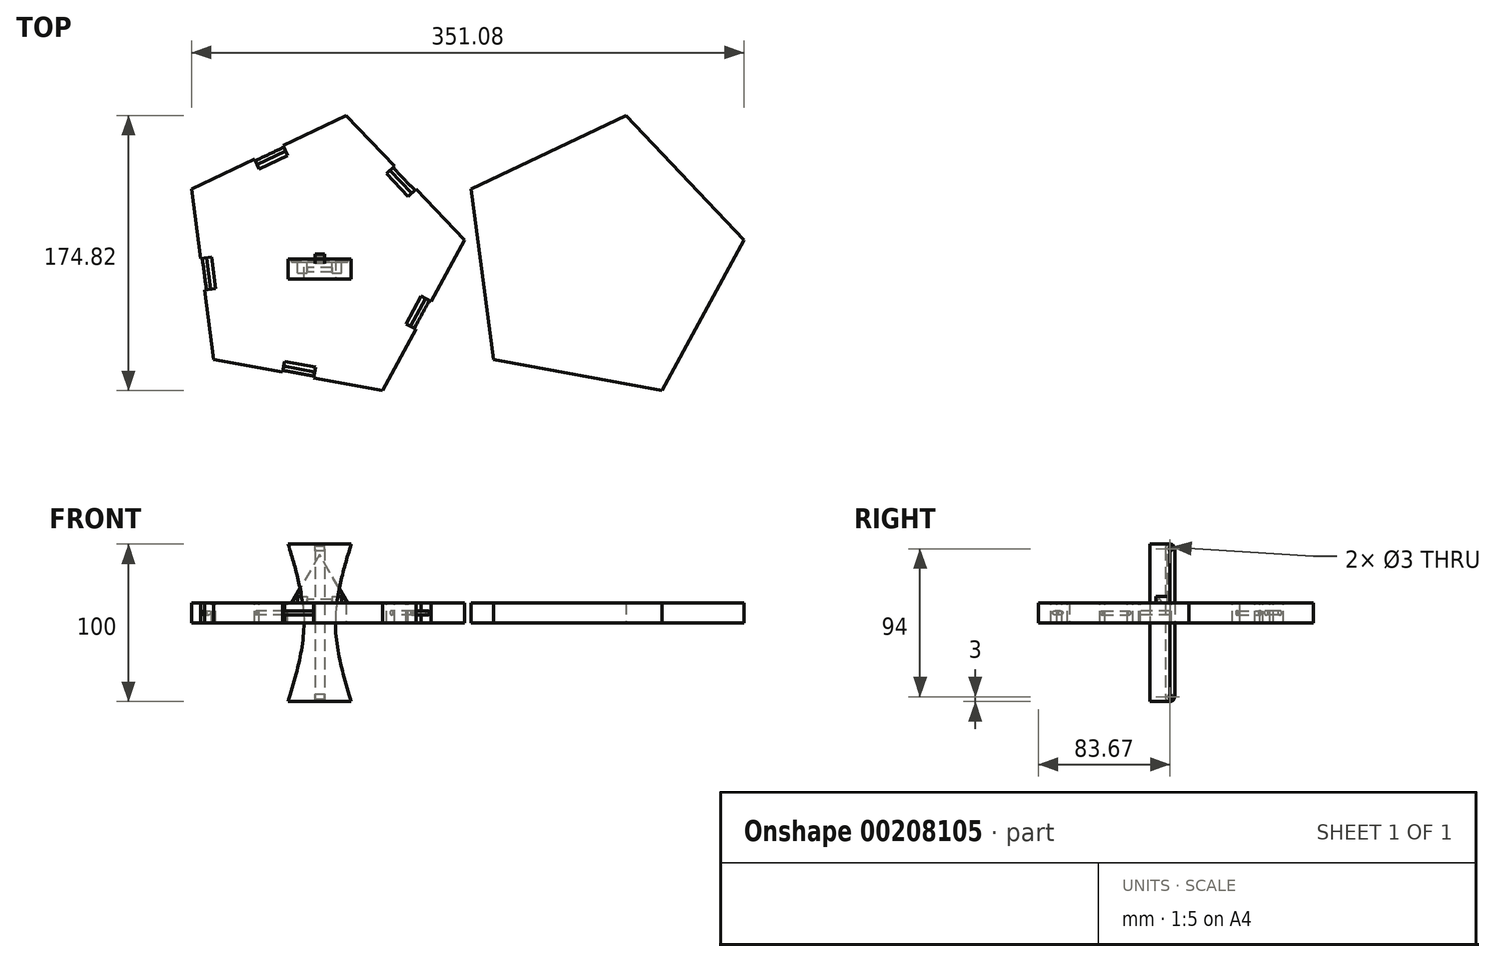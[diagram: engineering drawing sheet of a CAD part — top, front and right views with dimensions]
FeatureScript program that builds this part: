
annotation { "Feature Type Name" : "Feature", "Feature Type Description" : "" }
export const myFeature = defineFeature(function(context is Context, id is Id, definition is map)
    precondition{}
    {
        {
            var Q0;
            Q0=qCreatedBy(makeId("Top.planeOp"),FACE);
            var sketch = newSketch(context, id + "F0", { "sketchPlane" : qUnion([Q0])});
            skCircle(sketch, "E0.cCircle", {"center": v(0, 0) * mm, "radius": 75 * mm, "construction": true});
            skLineSegment(sketch, "E0.0", {"start": v(91.91, 12.1) * mm, "end": v(39.9, -83.67) * mm});
            skLineSegment(sketch, "E0.1", {"start": v(39.9, -83.67) * mm, "end": v(-67.25, -63.81) * mm});
            skLineSegment(sketch, "E0.2", {"start": v(-67.25, -63.81) * mm, "end": v(-81.47, 44.24) * mm});
            skLineSegment(sketch, "E0.3", {"start": v(-81.47, 44.24) * mm, "end": v(16.9, 91.15) * mm});
            skLineSegment(sketch, "E0.4", {"start": v(16.9, 91.15) * mm, "end": v(91.91, 12.1) * mm});
            skPoint(sketch, "E0.0.midPoint", {"position": v(65.91, -35.79) * mm});
            skSolve(sketch);
        }
        {
            var Q0;
            Q0=makeQuery(id+"F0.imprint","IMPRINT",FACE,{"disambiguationData":[TD([[makeQuery(id+"F0.imprint","IMPRINT",EDGE,{"derivedFrom":sQuery(id+"F0.wireOp",EDGE,"E0.0")}),-1.0]])]});
            extrude(context, id + "F1", {"entities" : qUnion([Q0]), "depth" : 12.7 * mm});
        }
        {
            var Q0;
            Q0=makeQuery(id+"F1.opExtrude","SWEPT_BODY",BODY,{"disambiguationData":[OSD([sQuery(id+"F0.wireOp",EDGE,"E0.0"),sQuery(id+"F0.wireOp",EDGE,"E0.1"),sQuery(id+"F0.wireOp",EDGE,"E0.2"),sQuery(id+"F0.wireOp",EDGE,"E0.3"),sQuery(id+"F0.wireOp",EDGE,"E0.4")])]});
            transform(context, id + "F2", {"entities" : qUnion([Q0]), "transformType" : TransformType.TRANSLATION_3D, "dx" : 177.7 * mm, "dy" : 0 * mm, "dz" : 0 * mm, "makeCopy" : true});
        }
        {
            var Q0;
            Q0=qCreatedBy(makeId("Front.planeOp"),FACE);
            var sketch = newSketch(context, id + "F3", { "sketchPlane" : qUnion([Q0])});
            skLineSegment(sketch, "E1", {"start": v(-25, 0) * mm, "end": v(25, 0) * mm});
            skLineSegment(sketch, "E2", {"start": v(25, 0) * mm, "end": v(0, 43.3) * mm});
            skLineSegment(sketch, "E3", {"start": v(0, 43.3) * mm, "end": v(-25, 0) * mm});
            skLineSegment(sketch, "E4", {"start": v(0, 43.3) * mm, "end": v(0, 0) * mm, "construction": true});
            skSolve(sketch);
        }
        {
            var Q0;
            Q0=makeQuery(id+"F3.imprint","IMPRINT",FACE,{"disambiguationData":[TD([[makeQuery(id+"F3.imprint","IMPRINT",EDGE,{"derivedFrom":sQuery(id+"F3.wireOp",EDGE,"E1")}),1.0]])]});
            extrude(context, id + "F4", {"entities" : qUnion([Q0]), "depth" : 2 * mm});
        }
        {
            var Q0;
            Q0=qCreatedBy(makeId("Right.planeOp"),FACE);
            var sketch = newSketch(context, id + "F5", { "sketchPlane" : qUnion([Q0])});
            skCircle(sketch, "E5", {"center": v(-7, 13.3) * mm, "radius": 1.5 * mm});
            skSolve(sketch);
        }
        {
            var Q0;
            Q0=makeQuery(id+"F4.opExtrude","CAP_FACE",FACE,{"disambiguationData":[OSD([sQuery(id+"F3.wireOp",EDGE,"E1"),sQuery(id+"F3.wireOp",EDGE,"E2"),sQuery(id+"F3.wireOp",EDGE,"E3")])],"isStart":false});
            var sketch = newSketch(context, id + "F6", { "sketchPlane" : qUnion([Q0])});
            skLineSegment(sketch, "E6.bottom", {"start": v(-14, 16.8) * mm, "end": v(-8, 16.8) * mm});
            skLineSegment(sketch, "E6.top", {"start": v(-14, 9.8) * mm, "end": v(-8, 9.8) * mm});
            skLineSegment(sketch, "E6.left", {"start": v(-14, 16.8) * mm, "end": v(-14, 9.8) * mm});
            skLineSegment(sketch, "E6.right", {"start": v(-8, 16.8) * mm, "end": v(-8, 9.8) * mm});
            skLineSegment(sketch, "E7.bottom", {"start": v(8, 16.8) * mm, "end": v(14, 16.8) * mm});
            skLineSegment(sketch, "E7.top", {"start": v(8, 9.8) * mm, "end": v(14, 9.8) * mm});
            skLineSegment(sketch, "E7.left", {"start": v(8, 16.8) * mm, "end": v(8, 9.8) * mm});
            skLineSegment(sketch, "E7.right", {"start": v(14, 16.8) * mm, "end": v(14, 9.8) * mm});
            skLineSegment(sketch, "E8", {"start": v(8, 13.3) * mm, "end": v(14, 13.3) * mm, "construction": true});
            skSolve(sketch);
        }
        {
            var Q0;
            Q0=makeQuery(id+"F6.imprint","IMPRINT",FACE,{"disambiguationData":[TD([[makeQuery(id+"F6.imprint","IMPRINT",EDGE,{"derivedFrom":sQuery(id+"F6.wireOp",EDGE,"E6.bottom")}),-1.0]])]});
            var Q1;
            Q1=makeQuery(id+"F6.imprint","IMPRINT",FACE,{"disambiguationData":[TD([[makeQuery(id+"F6.imprint","IMPRINT",EDGE,{"derivedFrom":sQuery(id+"F6.wireOp",EDGE,"E7.bottom")}),-1.0]])]});
            extrude(context, id + "F7", {"entities" : qUnion([Q0, Q1]), "operationType" : NewBodyOperationType.ADD, "depth" : 7 * mm});
        }
        {
            var Q0;
            Q0=makeQuery(id+"F5.imprint","IMPRINT",FACE,{"disambiguationData":[TD([[makeQuery(id+"F5.imprint","IMPRINT",EDGE,{"derivedFrom":sQuery(id+"F5.wireOp",EDGE,"E5")}),1.0]])]});
            extrude(context, id + "F8", {"entities" : qUnion([Q0]), "operationType" : NewBodyOperationType.ADD, "endBound" : BoundingType.SYMMETRIC, "depth" : 25 * mm});
        }
        {
            var Q0;
            Q0=makeQuery(id+"F1.opExtrude","CAP_FACE",FACE,{"disambiguationData":[OSD([sQuery(id+"F0.wireOp",EDGE,"E0.0"),sQuery(id+"F0.wireOp",EDGE,"E0.1"),sQuery(id+"F0.wireOp",EDGE,"E0.2"),sQuery(id+"F0.wireOp",EDGE,"E0.3"),sQuery(id+"F0.wireOp",EDGE,"E0.4")])],"isStart":false});
            var sketch = newSketch(context, id + "F9", { "sketchPlane" : qUnion([Q0])});
            skLineSegment(sketch, "E9", {"start": v(-75.66, 0.13) * mm, "end": v(-73.05, -19.7) * mm});
            skLineSegment(sketch, "E10", {"start": v(-73.05, -19.7) * mm, "end": v(-66.11, -18.79) * mm});
            skLineSegment(sketch, "E11", {"start": v(-66.11, -18.79) * mm, "end": v(-68.72, 1.04) * mm});
            skLineSegment(sketch, "E12", {"start": v(-75.66, 0.13) * mm, "end": v(-68.72, 1.04) * mm});
            skPoint(sketch, "E13.orphan", {"position": v(-73.05, 33.93) * mm});
            skLineSegment(sketch, "E14", {"start": v(-67.42, -8.87) * mm, "end": v(-74.36, -9.79) * mm, "construction": true});
            skLineSegment(sketch, "E15", {"start": v(-74.36, -9.79) * mm, "end": v(0, 0) * mm, "construction": true});
            skPoint(sketch, "E16.center", {"position": v(0, 0) * mm});
            skLineSegment(sketch, "E17.1.0", {"start": v(-23.5, -71.92) * mm, "end": v(-22.23, -65.04) * mm});
            skLineSegment(sketch, "E17.1.1", {"start": v(-2.56, -68.68) * mm, "end": v(-22.23, -65.04) * mm});
            skLineSegment(sketch, "E17.1.2", {"start": v(-3.84, -75.57) * mm, "end": v(-2.56, -68.68) * mm});
            skLineSegment(sketch, "E17.1.3", {"start": v(-23.5, -71.92) * mm, "end": v(-3.84, -75.57) * mm});
            skLineSegment(sketch, "E17.2.0", {"start": v(61.14, -44.58) * mm, "end": v(54.99, -41.24) * mm});
            skLineSegment(sketch, "E17.2.1", {"start": v(64.53, -23.66) * mm, "end": v(54.99, -41.24) * mm});
            skLineSegment(sketch, "E17.2.2", {"start": v(70.68, -27) * mm, "end": v(64.53, -23.66) * mm});
            skLineSegment(sketch, "E17.2.3", {"start": v(61.14, -44.58) * mm, "end": v(70.68, -27) * mm});
            skLineSegment(sketch, "E17.3.0", {"start": v(61.29, 44.37) * mm, "end": v(56.2, 39.55) * mm});
            skLineSegment(sketch, "E17.3.1", {"start": v(42.44, 54.06) * mm, "end": v(56.2, 39.55) * mm});
            skLineSegment(sketch, "E17.3.2", {"start": v(47.52, 58.88) * mm, "end": v(42.44, 54.06) * mm});
            skLineSegment(sketch, "E17.3.3", {"start": v(61.29, 44.37) * mm, "end": v(47.52, 58.88) * mm});
            skLineSegment(sketch, "E17.4.0", {"start": v(-23.26, 72) * mm, "end": v(-20.25, 65.68) * mm});
            skLineSegment(sketch, "E17.4.1", {"start": v(-38.3, 57.07) * mm, "end": v(-20.25, 65.68) * mm});
            skLineSegment(sketch, "E17.4.2", {"start": v(-41.31, 63.39) * mm, "end": v(-38.3, 57.07) * mm});
            skLineSegment(sketch, "E17.4.3", {"start": v(-23.26, 72) * mm, "end": v(-41.31, 63.39) * mm});
            skSolve(sketch);
        }
        {
            var Q0;
            Q0=makeQuery(id+"F9.imprint","IMPRINT",FACE,{"disambiguationData":[TD([[makeQuery(id+"F9.imprint","IMPRINT",EDGE,{"derivedFrom":sQuery(id+"F9.wireOp",EDGE,"E9")}),-1.0]])]});
            var Q1;
            Q1=makeQuery(id+"F9.imprint","IMPRINT",FACE,{"disambiguationData":[TD([[makeQuery(id+"F9.imprint","IMPRINT",EDGE,{"derivedFrom":sQuery(id+"F9.wireOp",EDGE,"E17.1.0")}),-1.0]])]});
            var Q2;
            Q2=makeQuery(id+"F9.imprint","IMPRINT",FACE,{"disambiguationData":[TD([[makeQuery(id+"F9.imprint","IMPRINT",EDGE,{"derivedFrom":sQuery(id+"F9.wireOp",EDGE,"E17.2.0")}),-1.0]])]});
            var Q3;
            Q3=makeQuery(id+"F9.imprint","IMPRINT",FACE,{"disambiguationData":[TD([[makeQuery(id+"F9.imprint","IMPRINT",EDGE,{"derivedFrom":sQuery(id+"F9.wireOp",EDGE,"E17.4.0")}),-1.0]])]});
            var Q4;
            Q4=makeQuery(id+"F9.imprint","IMPRINT",FACE,{"disambiguationData":[TD([[makeQuery(id+"F9.imprint","IMPRINT",EDGE,{"derivedFrom":sQuery(id+"F9.wireOp",EDGE,"E17.3.0")}),-1.0]])]});
            var Q5;
            Q5=makeQuery(id+"F1.opExtrude","CAP_FACE",FACE,{"disambiguationData":[OSD([sQuery(id+"F0.wireOp",EDGE,"E0.0"),sQuery(id+"F0.wireOp",EDGE,"E0.1"),sQuery(id+"F0.wireOp",EDGE,"E0.2"),sQuery(id+"F0.wireOp",EDGE,"E0.3"),sQuery(id+"F0.wireOp",EDGE,"E0.4")])],"isStart":true});
            extrude(context, id + "F10", {"entities" : qUnion([Q0, Q1, Q2, Q3, Q4]), "operationType" : NewBodyOperationType.REMOVE, "endBound" : BoundingType.UP_TO_SURFACE, "oppositeDirection" : true, "endBoundEntityFace" : qUnion([Q5]), "depth" : 25 * mm});
        }
        {
            var Q0;
            Q0=qCreatedBy(makeId("Right.planeOp"),FACE);
            var sketch = newSketch(context, id + "F11", { "sketchPlane" : qUnion([Q0])});
            skLineSegment(sketch, "E18", {"start": v(0, 0) * mm, "end": v(0, 99.53) * mm, "construction": true});
            skSolve(sketch);
        }
        {
            var Q0;
            Q0=makeQuery(id+"F10.boolean.opBoolean","COPY",FACE,{"derivedFrom":makeQuery(id+"F10.opExtrude","SWEPT_FACE",FACE,{"disambiguationData":[OSD([sQuery(id+"F9.wireOp",EDGE,"E10")])]})});
            var sketch = newSketch(context, id + "F12", { "sketchPlane" : qUnion([Q0])});
            skCircle(sketch, "E19", {"center": v(72.5, 6.35) * mm, "radius": 1.34 * mm});
            skLineSegment(sketch, "E20", {"start": v(75, 6.35) * mm, "end": v(68, 6.35) * mm, "construction": true});
            skSolve(sketch);
        }
        {
            var Q0;
            Q0=makeQuery(id+"F12.imprint","IMPRINT",FACE,{"disambiguationData":[TD([[makeQuery(id+"F12.imprint","IMPRINT",EDGE,{"derivedFrom":sQuery(id+"F12.wireOp",EDGE,"E19")}),1.0]])]});
            extrude(context, id + "F13", {"entities" : qUnion([Q0]), "depth" : 20 * mm});
        }
        {
            var Q0;
            Q0=makeQuery(id+"F13.opExtrude","SWEPT_BODY",BODY,{"disambiguationData":[OSD([sQuery(id+"F12.wireOp",EDGE,"E19")])]});
            var Q1;
            Q1=sQuery(id+"F11.wireOp",EDGE,"E18");
            circularPattern(context, id + "F14", {"entities" : qUnion([Q0]), "axis" : qUnion([Q1]), "angle" : 360 * degree, "instanceCount" : 5, "equalSpace" : true});
        }
        {
            var Q0;
            Q0=qCreatedBy(makeId("Right.planeOp"),FACE);
            var sketch = newSketch(context, id + "F15", { "sketchPlane" : qUnion([Q0])});
            skLineSegment(sketch, "E21.bottom", {"start": v(0, 50) * mm, "end": v(0, 50) * mm});
            skLineSegment(sketch, "E21.top", {"start": v(0, -50) * mm, "end": v(0, -50) * mm});
            skLineSegment(sketch, "E21.left", {"start": v(3, 47) * mm, "end": v(3, -47) * mm});
            skLineSegment(sketch, "E21.right", {"start": v(-3, 47) * mm, "end": v(-3, -47) * mm});
            skPoint(sketch, "E21.middle", {"position": v(0, 0) * mm});
            skPoint(sketch, "E22.visualSharp", {"position": v(3, 50) * mm});
            skArc(sketch, "E22.filletArc", {"start": v(3, 47) * mm, "mid": v(2.12, 49.12) * mm, "end": v(0, 50) * mm});
            skPoint(sketch, "E23.visualSharp", {"position": v(-3, 50) * mm});
            skArc(sketch, "E23.filletArc", {"start": v(0, 50) * mm, "mid": v(-2.12, 49.12) * mm, "end": v(-3, 47) * mm});
            skPoint(sketch, "E24.visualSharp", {"position": v(3, -50) * mm});
            skArc(sketch, "E24.filletArc", {"start": v(0, -50) * mm, "mid": v(2.12, -49.12) * mm, "end": v(3, -47) * mm});
            skPoint(sketch, "E25.visualSharp", {"position": v(-3, -50) * mm});
            skArc(sketch, "E25.filletArc", {"start": v(-3, -47) * mm, "mid": v(-2.12, -49.12) * mm, "end": v(0, -50) * mm});
            skCircle(sketch, "E26", {"center": v(0, -47) * mm, "radius": 1.5 * mm});
            skCircle(sketch, "E27", {"center": v(0, 47) * mm, "radius": 1.5 * mm});
            skSolve(sketch);
        }
        {
            var Q0;
            Q0=makeQuery(id+"F15.imprint","IMPRINT",FACE,{"disambiguationData":[TD([[makeQuery(id+"F15.imprint","IMPRINT",EDGE,{"derivedFrom":sQuery(id+"F15.wireOp",EDGE,"E21.left")}),-1.0]])]});
            extrude(context, id + "F16", {"entities" : qUnion([Q0]), "endBound" : BoundingType.SYMMETRIC, "depth" : 6 * mm});
        }
        {
            var Q0;
            Q0=qCreatedBy(makeId("Front.planeOp"),FACE);
            var sketch = newSketch(context, id + "F17", { "sketchPlane" : qUnion([Q0])});
            skLineSegment(sketch, "E28.bottom", {"start": v(-20, 50) * mm, "end": v(20, 50) * mm});
            skLineSegment(sketch, "E28.top", {"start": v(-20, -50) * mm, "end": v(20, -50) * mm});
            skLineSegment(sketch, "E28.left", {"start": v(-20, 50) * mm, "end": v(-20, -50) * mm, "construction": true});
            skLineSegment(sketch, "E28.right", {"start": v(20, 50) * mm, "end": v(20, -50) * mm, "construction": true});
            skPoint(sketch, "E28.middle", {"position": v(0, 0) * mm});
            skLineSegment(sketch, "E29", {"start": v(0, 0) * mm, "end": v(20, 0) * mm, "construction": true});
            skLineSegment(sketch, "E30", {"start": v(0, 0) * mm, "end": v(-20, 0) * mm, "construction": true});
            skLineSegment(sketch, "E31", {"start": v(10, 50) * mm, "end": v(10, -50) * mm, "construction": true});
            skLineSegment(sketch, "E32", {"start": v(-10, 50) * mm, "end": v(-10, -50) * mm, "construction": true});
            skFitSpline(sketch, "E33", {"points": [v(20, 50) * mm, v(10, 0) * mm, v(20, -50) * mm], "startDerivative": vector(-30, -100) * mm, "endDerivative": vector(30, -100) * mm});
            skFitSpline(sketch, "E34", {"points": [v(-20, 50) * mm, v(-10, 0) * mm, v(-20, -50) * mm], "startDerivative": vector(30, -100) * mm, "endDerivative": vector(-30, -100) * mm});
            skSolve(sketch);
        }
        {
            var Q0;
            Q0=makeQuery(id+"F17.imprint","IMPRINT",FACE,{"disambiguationData":[TD([[makeQuery(id+"F17.imprint","IMPRINT",EDGE,{"derivedFrom":sQuery(id+"F17.wireOp",EDGE,"E28.bottom")}),-1.0]])]});
            extrude(context, id + "F18", {"entities" : qUnion([Q0]), "depth" : 12.7 * mm});
        }
    });
